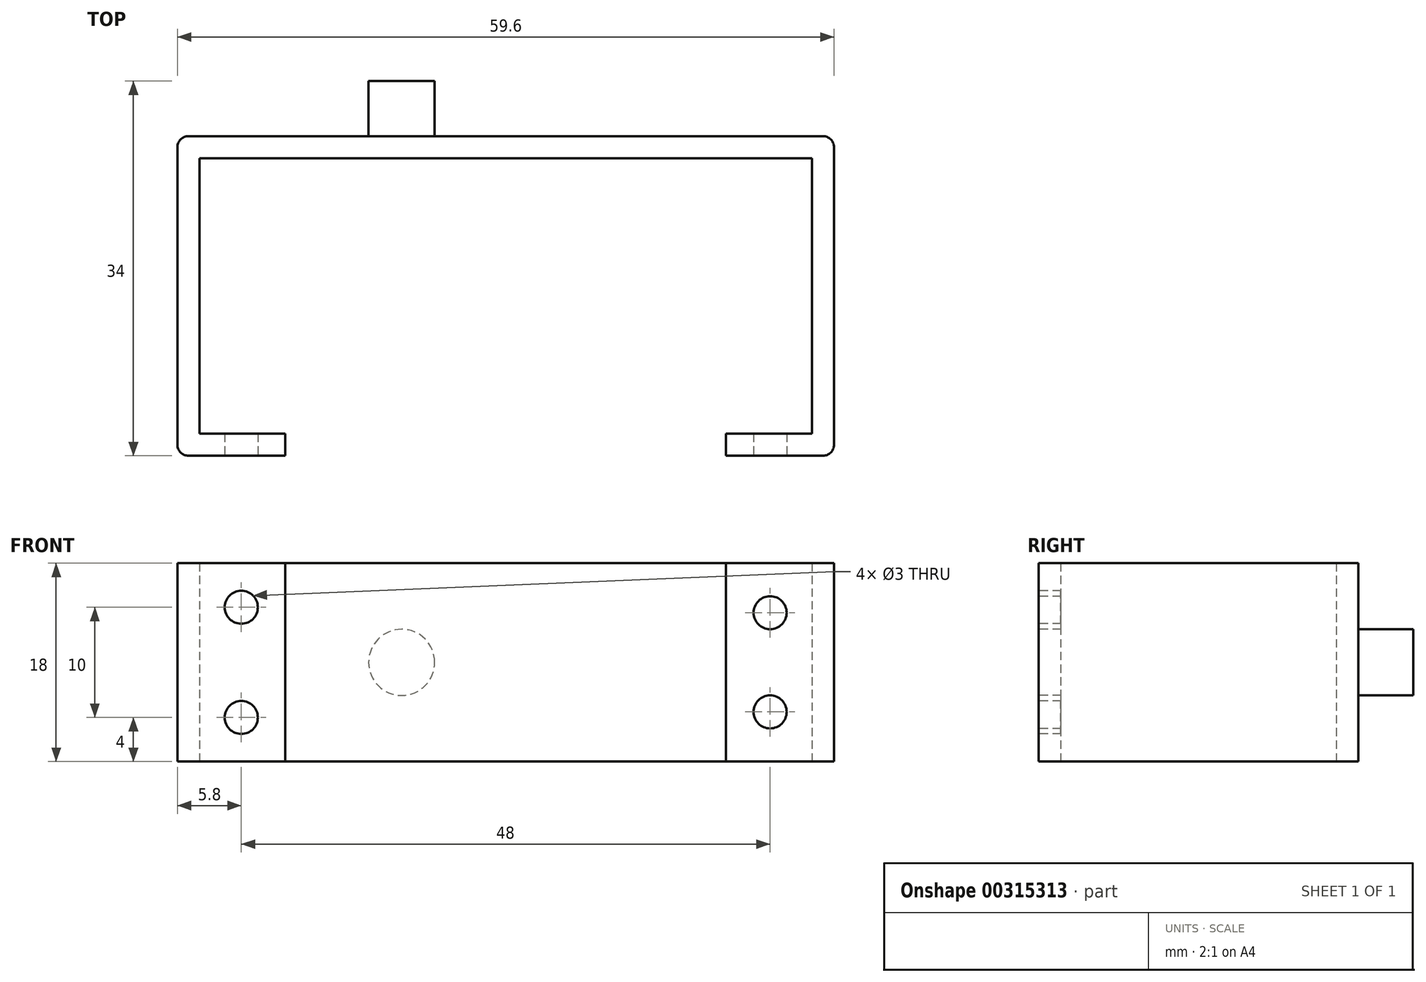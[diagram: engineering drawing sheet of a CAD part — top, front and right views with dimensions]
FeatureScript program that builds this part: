
annotation { "Feature Type Name" : "Feature", "Feature Type Description" : "" }
export const myFeature = defineFeature(function(context is Context, id is Id, definition is map)
    precondition{}
    {
        {
            var Q0;
            Q0=qCreatedBy(makeId("Front.planeOp"),FACE);
            var sketch = newSketch(context, id + "F0", { "sketchPlane" : qUnion([Q0])});
            skPoint(sketch, "E0", {"position": v(20, 0) * mm});
            skPoint(sketch, "E1", {"position": v(-20, 0) * mm});
            skPoint(sketch, "E2", {"position": v(-24, 0) * mm});
            skPoint(sketch, "E3", {"position": v(24, 0) * mm});
            skLineSegment(sketch, "E4", {"start": v(-24, 0) * mm, "end": v(-24, 9) * mm});
            skLineSegment(sketch, "E5", {"start": v(24, 0) * mm, "end": v(24, 9) * mm});
            skLineSegment(sketch, "E6", {"start": v(-24, 0) * mm, "end": v(-24, -9) * mm});
            skLineSegment(sketch, "E7", {"start": v(24, 0) * mm, "end": v(24, -9) * mm});
            skPoint(sketch, "E8", {"position": v(-24, 5) * mm});
            skPoint(sketch, "E9", {"position": v(-24, -5) * mm});
            skPoint(sketch, "E10", {"position": v(24, 4.5) * mm});
            skPoint(sketch, "E11", {"position": v(24, -4.5) * mm});
            skCircle(sketch, "E12", {"center": v(-24, 5) * mm, "radius": 1.75 * mm});
            skCircle(sketch, "E13", {"center": v(-24, -5) * mm, "radius": 1.75 * mm});
            skCircle(sketch, "E14", {"center": v(24, 4.5) * mm, "radius": 1.75 * mm});
            skCircle(sketch, "E15", {"center": v(24, -4.5) * mm, "radius": 1.75 * mm});
            skPoint(sketch, "E16", {"position": v(-10, 0) * mm});
            skCircle(sketch, "E17", {"center": v(-10, 0) * mm, "radius": 3 * mm});
            skPoint(sketch, "E18", {"position": v(-27.8, 0) * mm});
            skPoint(sketch, "E19", {"position": v(27.8, 0) * mm});
            skLineSegment(sketch, "E20.bottom", {"start": v(-27.8, 0) * mm, "end": v(27.8, 0) * mm});
            skLineSegment(sketch, "E20.top", {"start": v(-27.8, 9) * mm, "end": v(27.8, 9) * mm});
            skLineSegment(sketch, "E20.left", {"start": v(-27.8, 0) * mm, "end": v(-27.8, 9) * mm});
            skLineSegment(sketch, "E20.right", {"start": v(27.8, 0) * mm, "end": v(27.8, 9) * mm});
            skLineSegment(sketch, "E21.top", {"start": v(-27.8, -9) * mm, "end": v(27.8, -9) * mm});
            skLineSegment(sketch, "E21.left", {"start": v(-27.8, 0) * mm, "end": v(-27.8, -9) * mm});
            skLineSegment(sketch, "E21.right", {"start": v(27.8, 0) * mm, "end": v(27.8, -9) * mm});
            skLineSegment(sketch, "E22", {"start": v(-20, 0) * mm, "end": v(-20, 9) * mm});
            skLineSegment(sketch, "E23", {"start": v(-20, 0) * mm, "end": v(-20, -9) * mm});
            skLineSegment(sketch, "E24", {"start": v(20, 0) * mm, "end": v(20, 9) * mm});
            skLineSegment(sketch, "E25", {"start": v(20, 0) * mm, "end": v(20, -9) * mm});
            skCircle(sketch, "E26", {"center": v(-24, 5) * mm, "radius": 1.5 * mm});
            skCircle(sketch, "E27", {"center": v(-24, -5) * mm, "radius": 1.5 * mm});
            skCircle(sketch, "E28", {"center": v(24, 4.5) * mm, "radius": 1.5 * mm});
            skCircle(sketch, "E29", {"center": v(24, -4.5) * mm, "radius": 1.5 * mm});
            skSolve(sketch);
        }
        {
            var Q0;
            Q0=qCreatedBy(makeId("Top.planeOp"),FACE);
            var sketch = newSketch(context, id + "F1", { "sketchPlane" : qUnion([Q0])});
            skPoint(sketch, "E30", {"position": v(-20, 0) * mm});
            skPoint(sketch, "E31", {"position": v(-27.8, 0) * mm});
            skPoint(sketch, "E32", {"position": v(20, 0) * mm});
            skPoint(sketch, "E33", {"position": v(27.8, 0) * mm});
            skLineSegment(sketch, "E34.bottom", {"start": v(-20, 0) * mm, "end": v(-27.8, 0) * mm});
            skLineSegment(sketch, "E34.top", {"start": v(-20, 2) * mm, "end": v(-27.8, 2) * mm});
            skLineSegment(sketch, "E34.left", {"start": v(-20, 0) * mm, "end": v(-20, 2) * mm});
            skLineSegment(sketch, "E34.right", {"start": v(-27.8, 0) * mm, "end": v(-27.8, 2) * mm});
            skLineSegment(sketch, "E35.bottom", {"start": v(20, 0) * mm, "end": v(27.8, 0) * mm});
            skLineSegment(sketch, "E35.top", {"start": v(20, 2) * mm, "end": v(27.8, 2) * mm});
            skLineSegment(sketch, "E35.left", {"start": v(20, 0) * mm, "end": v(20, 2) * mm});
            skLineSegment(sketch, "E35.right", {"start": v(27.8, 0) * mm, "end": v(27.8, 2) * mm});
            skLineSegment(sketch, "E36.bottom", {"start": v(-27.8, 0) * mm, "end": v(-25.8, 0) * mm});
            skLineSegment(sketch, "E36.top", {"start": v(-27.8, 27) * mm, "end": v(-25.8, 27) * mm});
            skLineSegment(sketch, "E36.left", {"start": v(-27.8, 0) * mm, "end": v(-27.8, 27) * mm});
            skLineSegment(sketch, "E36.right", {"start": v(-25.8, 0) * mm, "end": v(-25.8, 27) * mm});
            skLineSegment(sketch, "E37.bottom", {"start": v(27.8, 0) * mm, "end": v(25.8, 0) * mm});
            skLineSegment(sketch, "E37.top", {"start": v(27.8, 27) * mm, "end": v(25.8, 27) * mm});
            skLineSegment(sketch, "E37.left", {"start": v(27.8, 0) * mm, "end": v(27.8, 27) * mm});
            skLineSegment(sketch, "E37.right", {"start": v(25.8, 0) * mm, "end": v(25.8, 27) * mm});
            skLineSegment(sketch, "E38.bottom", {"start": v(-27.8, 27) * mm, "end": v(27.8, 27) * mm});
            skLineSegment(sketch, "E38.top", {"start": v(-27.8, 29) * mm, "end": v(27.8, 29) * mm});
            skLineSegment(sketch, "E38.left", {"start": v(-27.8, 27) * mm, "end": v(-27.8, 29) * mm});
            skLineSegment(sketch, "E38.right", {"start": v(27.8, 27) * mm, "end": v(27.8, 29) * mm});
            skLineSegment(sketch, "E39.bottom", {"start": v(-27.8, 29) * mm, "end": v(-29.8, 29) * mm});
            skLineSegment(sketch, "E39.top", {"start": v(-27.8, 0) * mm, "end": v(-29.8, 0) * mm});
            skLineSegment(sketch, "E39.left", {"start": v(-27.8, 29) * mm, "end": v(-27.8, 0) * mm});
            skLineSegment(sketch, "E39.right", {"start": v(-29.8, 29) * mm, "end": v(-29.8, 0) * mm});
            skLineSegment(sketch, "E40.bottom", {"start": v(27.8, 29) * mm, "end": v(29.8, 29) * mm});
            skLineSegment(sketch, "E40.top", {"start": v(27.8, 0) * mm, "end": v(29.8, 0) * mm});
            skLineSegment(sketch, "E40.left", {"start": v(27.8, 29) * mm, "end": v(27.8, 0) * mm});
            skLineSegment(sketch, "E40.right", {"start": v(29.8, 29) * mm, "end": v(29.8, 0) * mm});
            skSolve(sketch);
        }
        {
            var Q0;
            {var subQ0=sQuery(id+"F1.wireOp",EDGE,"E35.bottom");Q0=makeQuery(id+"F1.imprint","IMPRINT",FACE,{"disambiguationData":[TD([[makeQuery(id+"F1.imprint","IMPRINT",EDGE,{"derivedFrom":subQ0}),1.0]])]});}
            var Q1;
            {var subQ5=sQuery(id+"F1.wireOp",EDGE,"E37.bottom");Q1=makeQuery(id+"F1.imprint","IMPRINT",FACE,{"disambiguationData":[TD([[makeQuery(id+"F1.imprint","IMPRINT",EDGE,{"derivedFrom":subQ5}),-1.0]])]});}
            var Q2;
            {var subQ3=sQuery(id+"F1.wireOp",EDGE,"E39.bottom");Q2=makeQuery(id+"F1.imprint","IMPRINT",FACE,{"disambiguationData":[TD([[makeQuery(id+"F1.imprint","IMPRINT",EDGE,{"derivedFrom":subQ3}),1.0]])]});}
            var Q3;
            {var subQ3=sQuery(id+"F1.wireOp",EDGE,"E40.bottom");Q3=makeQuery(id+"F1.imprint","IMPRINT",FACE,{"disambiguationData":[TD([[makeQuery(id+"F1.imprint","IMPRINT",EDGE,{"derivedFrom":subQ3}),-1.0]])]});}
            var Q4;
            {var subQ0=sQuery(id+"F1.wireOp",EDGE,"E38.top");Q4=makeQuery(id+"F1.imprint","IMPRINT",FACE,{"disambiguationData":[TD([[makeQuery(id+"F1.imprint","IMPRINT",EDGE,{"derivedFrom":subQ0}),-1.0]])]});}
            var Q5;
            {var subQ5=sQuery(id+"F1.wireOp",EDGE,"E36.bottom");Q5=makeQuery(id+"F1.imprint","IMPRINT",FACE,{"disambiguationData":[TD([[makeQuery(id+"F1.imprint","IMPRINT",EDGE,{"derivedFrom":subQ5}),1.0]])]});}
            var Q6;
            {var subQ0=sQuery(id+"F1.wireOp",EDGE,"E34.bottom");Q6=makeQuery(id+"F1.imprint","IMPRINT",FACE,{"disambiguationData":[TD([[makeQuery(id+"F1.imprint","IMPRINT",EDGE,{"derivedFrom":subQ0}),-1.0]])]});}
            extrude(context, id + "F2", {"entities" : qUnion([Q0, Q1, Q2, Q3, Q4, Q5, Q6]), "endBound" : BoundingType.SYMMETRIC, "depth" : 18 * mm});
        }
        {
            var Q0;
            {var subQ0=sQuery(id+"F0.wireOp",EDGE,"E26");var subQ1=sQuery(id+"F0.wireOp",EDGE,"E4");var subQ2=makeQuery(id+"F0.imprint","INTERSECT",VERTEX,{"disambiguationData":[OD(0.0)],"derivedFrom":[subQ1,subQ0]});Q0=makeQuery(id+"F0.imprint","IMPRINT",FACE,{"disambiguationData":[TD([[makeQuery(id+"F0.imprint","IMPRINT",EDGE,{"disambiguationData":[TD([[subQ2,-1.0]])],"derivedFrom":subQ1}),1.0]])]});}
            var Q1;
            {var subQ0=sQuery(id+"F0.wireOp",EDGE,"E26");var subQ1=sQuery(id+"F0.wireOp",EDGE,"E4");var subQ2=makeQuery(id+"F0.imprint","INTERSECT",VERTEX,{"disambiguationData":[OD(0.0)],"derivedFrom":[subQ1,subQ0]});Q1=makeQuery(id+"F0.imprint","IMPRINT",FACE,{"disambiguationData":[TD([[makeQuery(id+"F0.imprint","IMPRINT",EDGE,{"disambiguationData":[TD([[subQ2,-1.0]])],"derivedFrom":subQ1}),-1.0]])]});}
            var Q2;
            {var subQ0=sQuery(id+"F0.wireOp",EDGE,"E27");var subQ1=sQuery(id+"F0.wireOp",EDGE,"E6");var subQ2=makeQuery(id+"F0.imprint","INTERSECT",VERTEX,{"disambiguationData":[OD(0.0)],"derivedFrom":[subQ1,subQ0]});Q2=makeQuery(id+"F0.imprint","IMPRINT",FACE,{"disambiguationData":[TD([[makeQuery(id+"F0.imprint","IMPRINT",EDGE,{"disambiguationData":[TD([[subQ2,-1.0]])],"derivedFrom":subQ1}),-1.0]])]});}
            var Q3;
            {var subQ0=sQuery(id+"F0.wireOp",EDGE,"E27");var subQ1=sQuery(id+"F0.wireOp",EDGE,"E6");var subQ2=makeQuery(id+"F0.imprint","INTERSECT",VERTEX,{"disambiguationData":[OD(0.0)],"derivedFrom":[subQ1,subQ0]});Q3=makeQuery(id+"F0.imprint","IMPRINT",FACE,{"disambiguationData":[TD([[makeQuery(id+"F0.imprint","IMPRINT",EDGE,{"disambiguationData":[TD([[subQ2,-1.0]])],"derivedFrom":subQ1}),1.0]])]});}
            var Q4;
            {var subQ0=sQuery(id+"F0.wireOp",EDGE,"E28");var subQ1=sQuery(id+"F0.wireOp",EDGE,"E5");var subQ2=makeQuery(id+"F0.imprint","INTERSECT",VERTEX,{"disambiguationData":[OD(0.0)],"derivedFrom":[subQ1,subQ0]});Q4=makeQuery(id+"F0.imprint","IMPRINT",FACE,{"disambiguationData":[TD([[makeQuery(id+"F0.imprint","IMPRINT",EDGE,{"disambiguationData":[TD([[subQ2,-1.0]])],"derivedFrom":subQ1}),1.0]])]});}
            var Q5;
            {var subQ0=sQuery(id+"F0.wireOp",EDGE,"E28");var subQ1=sQuery(id+"F0.wireOp",EDGE,"E5");var subQ2=makeQuery(id+"F0.imprint","INTERSECT",VERTEX,{"disambiguationData":[OD(0.0)],"derivedFrom":[subQ1,subQ0]});Q5=makeQuery(id+"F0.imprint","IMPRINT",FACE,{"disambiguationData":[TD([[makeQuery(id+"F0.imprint","IMPRINT",EDGE,{"disambiguationData":[TD([[subQ2,-1.0]])],"derivedFrom":subQ1}),-1.0]])]});}
            var Q6;
            {var subQ0=sQuery(id+"F0.wireOp",EDGE,"E29");var subQ1=sQuery(id+"F0.wireOp",EDGE,"E7");var subQ2=makeQuery(id+"F0.imprint","INTERSECT",VERTEX,{"disambiguationData":[OD(0.0)],"derivedFrom":[subQ1,subQ0]});Q6=makeQuery(id+"F0.imprint","IMPRINT",FACE,{"disambiguationData":[TD([[makeQuery(id+"F0.imprint","IMPRINT",EDGE,{"disambiguationData":[TD([[subQ2,-1.0]])],"derivedFrom":subQ1}),1.0]])]});}
            var Q7;
            {var subQ0=sQuery(id+"F0.wireOp",EDGE,"E29");var subQ1=sQuery(id+"F0.wireOp",EDGE,"E7");var subQ2=makeQuery(id+"F0.imprint","INTERSECT",VERTEX,{"disambiguationData":[OD(0.0)],"derivedFrom":[subQ1,subQ0]});Q7=makeQuery(id+"F0.imprint","IMPRINT",FACE,{"disambiguationData":[TD([[makeQuery(id+"F0.imprint","IMPRINT",EDGE,{"disambiguationData":[TD([[subQ2,-1.0]])],"derivedFrom":subQ1}),-1.0]])]});}
            extrude(context, id + "F3", {"entities" : qUnion([Q0, Q1, Q2, Q3, Q4, Q5, Q6, Q7]), "operationType" : NewBodyOperationType.REMOVE, "oppositeDirection" : true, "depth" : 25 * mm});
        }
        {
            var Q0;
            Q0=makeQuery(id+"F2.opExtrude","SWEPT_EDGE",EDGE,{"disambiguationData":[OSD([sQuery(id+"F1.wireOp",EDGE,"E39.top"),sQuery(id+"F1.wireOp",EDGE,"E39.right")])]});
            var Q1;
            Q1=makeQuery(id+"F2.opExtrude","SWEPT_EDGE",EDGE,{"disambiguationData":[OSD([sQuery(id+"F1.wireOp",EDGE,"E40.top"),sQuery(id+"F1.wireOp",EDGE,"E40.right")])]});
            var Q2;
            Q2=makeQuery(id+"F2.opExtrude","SWEPT_EDGE",EDGE,{"disambiguationData":[OSD([sQuery(id+"F1.wireOp",EDGE,"E40.bottom"),sQuery(id+"F1.wireOp",EDGE,"E40.right")])]});
            var Q3;
            Q3=makeQuery(id+"F2.opExtrude","SWEPT_EDGE",EDGE,{"disambiguationData":[OSD([sQuery(id+"F1.wireOp",EDGE,"E39.bottom"),sQuery(id+"F1.wireOp",EDGE,"E39.right")])]});
            fillet(context, id + "F4", {"entities" : qUnion([Q0, Q1, Q2, Q3]), "radius" : 1 * mm, "tangentPropagation" : true, "allowEdgeOverflow" : false});
        }
        {
            var Q0;
            Q0=makeQuery(id+"F2.opExtrude","SWEPT_FACE",FACE,{"disambiguationData":[OSD([sQuery(id+"F1.wireOp",EDGE,"E38.bottom")])]});
            var sketch = newSketch(context, id + "F5", { "sketchPlane" : qUnion([Q0])});
            skPoint(sketch, "E41", {"position": v(20.56, 0) * mm});
            skPoint(sketch, "E42", {"position": v(-19.44, 0) * mm});
            skPoint(sketch, "E43", {"position": v(-23.44, 0) * mm});
            skPoint(sketch, "E44", {"position": v(24.56, 0) * mm});
            skLineSegment(sketch, "E45", {"start": v(-23.44, 0) * mm, "end": v(-23.44, 9) * mm});
            skLineSegment(sketch, "E46", {"start": v(24.56, 0) * mm, "end": v(24.56, 9) * mm});
            skLineSegment(sketch, "E47", {"start": v(-23.44, 0) * mm, "end": v(-23.44, -9) * mm});
            skLineSegment(sketch, "E48", {"start": v(24.56, 0) * mm, "end": v(24.56, -9) * mm});
            skPoint(sketch, "E49", {"position": v(-23.44, 5) * mm});
            skPoint(sketch, "E50", {"position": v(-23.44, -5) * mm});
            skPoint(sketch, "E51", {"position": v(24.56, 4.5) * mm});
            skPoint(sketch, "E52", {"position": v(24.56, -4.5) * mm});
            skCircle(sketch, "E53", {"center": v(-23.44, 5) * mm, "radius": 1.75 * mm});
            skCircle(sketch, "E54", {"center": v(-23.44, -5) * mm, "radius": 1.75 * mm});
            skCircle(sketch, "E55", {"center": v(24.56, 4.5) * mm, "radius": 1.75 * mm});
            skCircle(sketch, "E56", {"center": v(24.56, -4.5) * mm, "radius": 1.75 * mm});
            skPoint(sketch, "E57", {"position": v(-9.44, 0) * mm});
            skCircle(sketch, "E58", {"center": v(-9.44, 0) * mm, "radius": 3 * mm});
            skPoint(sketch, "E59", {"position": v(-27.24, 0) * mm});
            skPoint(sketch, "E60", {"position": v(28.36, 0) * mm});
            skLineSegment(sketch, "E61.bottom", {"start": v(-27.24, 0) * mm, "end": v(28.36, 0) * mm});
            skLineSegment(sketch, "E61.top", {"start": v(-27.24, 9) * mm, "end": v(28.36, 9) * mm});
            skLineSegment(sketch, "E61.left", {"start": v(-27.24, 0) * mm, "end": v(-27.24, 9) * mm});
            skLineSegment(sketch, "E61.right", {"start": v(28.36, 0) * mm, "end": v(28.36, 9) * mm});
            skLineSegment(sketch, "E62.top", {"start": v(-27.24, -9) * mm, "end": v(28.36, -9) * mm});
            skLineSegment(sketch, "E62.left", {"start": v(-27.24, 0) * mm, "end": v(-27.24, -9) * mm});
            skLineSegment(sketch, "E62.right", {"start": v(28.36, 0) * mm, "end": v(28.36, -9) * mm});
            skLineSegment(sketch, "E63", {"start": v(-19.44, 0) * mm, "end": v(-19.44, 9) * mm});
            skLineSegment(sketch, "E64", {"start": v(-19.44, 0) * mm, "end": v(-19.44, -9) * mm});
            skLineSegment(sketch, "E65", {"start": v(20.56, 0) * mm, "end": v(20.56, 9) * mm});
            skLineSegment(sketch, "E66", {"start": v(20.56, 0) * mm, "end": v(20.56, -9) * mm});
            skCircle(sketch, "E67", {"center": v(-23.44, 5) * mm, "radius": 1.5 * mm});
            skCircle(sketch, "E68", {"center": v(-23.44, -5) * mm, "radius": 1.5 * mm});
            skCircle(sketch, "E69", {"center": v(24.56, 4.5) * mm, "radius": 1.5 * mm});
            skCircle(sketch, "E70", {"center": v(24.56, -4.5) * mm, "radius": 1.5 * mm});
            skSolve(sketch);
        }
        {
            var Q0;
            {var subQ0=sQuery(id+"F5.wireOp",EDGE,"E61.bottom");var subQ1=sQuery(id+"F5.wireOp",EDGE,"E58");var subQ2=makeQuery(id+"F5.imprint","INTERSECT",VERTEX,{"disambiguationData":[OD(0.0)],"derivedFrom":[subQ1,subQ0]});Q0=makeQuery(id+"F5.imprint","IMPRINT",FACE,{"disambiguationData":[TD([[makeQuery(id+"F5.imprint","IMPRINT",EDGE,{"disambiguationData":[TD([[subQ2,-1.0]])],"derivedFrom":subQ1}),1.0]])]});}
            var Q1;
            {var subQ0=sQuery(id+"F5.wireOp",EDGE,"E61.bottom");var subQ1=sQuery(id+"F5.wireOp",EDGE,"E58");var subQ2=makeQuery(id+"F5.imprint","INTERSECT",VERTEX,{"disambiguationData":[OD(0.0)],"derivedFrom":[subQ1,subQ0]});Q1=makeQuery(id+"F5.imprint","IMPRINT",FACE,{"disambiguationData":[TD([[makeQuery(id+"F5.imprint","IMPRINT",EDGE,{"disambiguationData":[TD([[subQ2,1.0]])],"derivedFrom":subQ1}),1.0]])]});}
            extrude(context, id + "F6", {"entities" : qUnion([Q0, Q1]), "operationType" : NewBodyOperationType.ADD, "oppositeDirection" : true, "depth" : 7 * mm});
        }
    });
